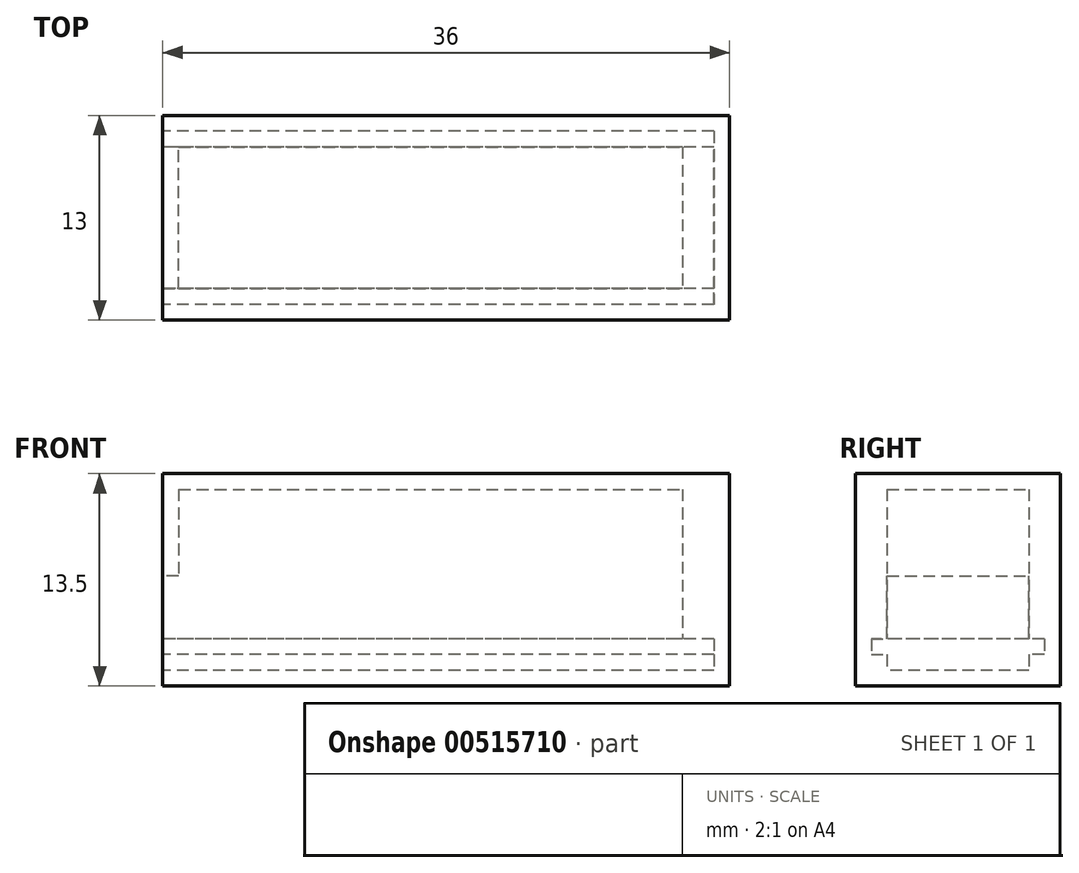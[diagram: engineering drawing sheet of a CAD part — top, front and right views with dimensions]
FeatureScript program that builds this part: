
annotation { "Feature Type Name" : "Feature", "Feature Type Description" : "" }
export const myFeature = defineFeature(function(context is Context, id is Id, definition is map)
    precondition{}
    {
        {
            var Q0;
            Q0=qCreatedBy(makeId("Top.planeOp"),FACE);
            var sketch = newSketch(context, id + "F0", { "sketchPlane" : qUnion([Q0])});
            skLineSegment(sketch, "E0.bottom", {"start": v(-27.77, -4.5) * mm, "end": v(4.23, -4.5) * mm});
            skLineSegment(sketch, "E0.top", {"start": v(-27.77, 4.5) * mm, "end": v(4.23, 4.5) * mm});
            skLineSegment(sketch, "E0.left", {"start": v(-27.77, -4.5) * mm, "end": v(-27.77, 4.5) * mm});
            skLineSegment(sketch, "E0.right", {"start": v(4.23, -4.5) * mm, "end": v(4.23, 4.5) * mm});
            skLineSegment(sketch, "E1.bottom", {"start": v(-28.77, -6.5) * mm, "end": v(7.23, -6.5) * mm});
            skLineSegment(sketch, "E1.top", {"start": v(-28.77, 6.5) * mm, "end": v(7.23, 6.5) * mm});
            skLineSegment(sketch, "E1.left", {"start": v(-28.77, -6.5) * mm, "end": v(-28.77, 6.5) * mm});
            skLineSegment(sketch, "E1.right", {"start": v(7.23, -6.5) * mm, "end": v(7.23, 6.5) * mm});
            skLineSegment(sketch, "E2", {"start": v(-28.77, 0) * mm, "end": v(7.23, 0) * mm, "construction": true});
            skLineSegment(sketch, "E3", {"start": v(-27.77, -4.5) * mm, "end": v(-28.77, -4.5) * mm});
            skLineSegment(sketch, "E4", {"start": v(-27.77, 4.5) * mm, "end": v(-28.77, 4.5) * mm});
            skSolve(sketch);
        }
        {
            var Q0;
            Q0=makeQuery(id+"F0.imprint","IMPRINT",FACE,{"disambiguationData":[TD([[makeQuery(id+"F0.imprint","IMPRINT",EDGE,{"derivedFrom":sQuery(id+"F0.wireOp",EDGE,"E0.bottom")}),-1.0]])]});
            var Q1;
            Q1=makeQuery(id+"F0.imprint","IMPRINT",FACE,{"disambiguationData":[TD([[makeQuery(id+"F0.imprint","IMPRINT",EDGE,{"derivedFrom":sQuery(id+"F0.wireOp",EDGE,"E0.bottom")}),1.0]])]});
            var Q2;
            Q2=makeQuery(id+"F0.imprint","IMPRINT",FACE,{"disambiguationData":[TD([[makeQuery(id+"F0.imprint","IMPRINT",EDGE,{"derivedFrom":sQuery(id+"F0.wireOp",EDGE,"E0.left")}),1.0]])]});
            extrude(context, id + "F1", {"entities" : qUnion([Q0, Q1, Q2]), "depth" : 6.5 * mm, "offsetDistance" : 25 * mm});
        }
        {
            var Q0;
            Q0=makeQuery(id+"F0.imprint","IMPRINT",FACE,{"disambiguationData":[TD([[makeQuery(id+"F0.imprint","IMPRINT",EDGE,{"derivedFrom":sQuery(id+"F0.wireOp",EDGE,"E0.bottom")}),1.0]])]});
            extrude(context, id + "F2", {"entities" : qUnion([Q0]), "operationType" : NewBodyOperationType.REMOVE, "depth" : 5.5 * mm, "offsetDistance" : 25 * mm});
        }
        {
            var Q0;
            Q0=makeQuery(id+"F0.imprint","IMPRINT",FACE,{"disambiguationData":[TD([[makeQuery(id+"F0.imprint","IMPRINT",EDGE,{"derivedFrom":sQuery(id+"F0.wireOp",EDGE,"E0.bottom")}),-1.0]])]});
            extrude(context, id + "F3", {"entities" : qUnion([Q0]), "operationType" : NewBodyOperationType.ADD, "oppositeDirection" : true, "depth" : 7 * mm, "offsetDistance" : 25 * mm});
        }
        {
            var Q0;
            {var subQ0=sQuery(id+"F0.wireOp",EDGE,"E1.left");Q0=makeQuery(id+"F3.boolean.opBoolean","MERGE",FACE,{"derivedFrom":[makeQuery(id+"F1.opExtrude","SWEPT_FACE",FACE,{"disambiguationData":[OSD([subQ0])]}),makeQuery(id+"F3.opExtrude","SWEPT_FACE",FACE,{"disambiguationData":[OSD([subQ0]),TDD([makeQuery(id+"F0.imprint","IMPRINT",EDGE,{"disambiguationData":[TD([[makeQuery(id+"F0.imprint","INTERSECT",VERTEX,{"derivedFrom":[sQuery(id+"F0.wireOp",EDGE,"E1.bottom"),subQ0]}),-1.0]])],"derivedFrom":subQ0})])]}),makeQuery(id+"F3.opExtrude","SWEPT_FACE",FACE,{"disambiguationData":[OSD([subQ0]),TDD([makeQuery(id+"F0.imprint","IMPRINT",EDGE,{"disambiguationData":[TD([[makeQuery(id+"F0.imprint","INTERSECT",VERTEX,{"derivedFrom":[sQuery(id+"F0.wireOp",EDGE,"E1.top"),subQ0]}),1.0]])],"derivedFrom":subQ0})])]})]});}
            var sketch = newSketch(context, id + "F4", { "sketchPlane" : qUnion([Q0])});
            skLineSegment(sketch, "E5.bottom", {"start": v(-5.5, -4) * mm, "end": v(-4.5, -4) * mm});
            skLineSegment(sketch, "E5.top", {"start": v(-5.5, -5) * mm, "end": v(-4.5, -5) * mm});
            skLineSegment(sketch, "E5.left", {"start": v(-5.5, -4) * mm, "end": v(-5.5, -5) * mm});
            skLineSegment(sketch, "E5.right", {"start": v(-4.5, -4) * mm, "end": v(-4.5, -5) * mm});
            skLineSegment(sketch, "E6", {"start": v(0, 0) * mm, "end": v(0, -9.1) * mm, "construction": true});
            skPoint(sketch, "E6.endSnap0", {"position": v(0, 0) * mm});
            skLineSegment(sketch, "E7.bottom", {"start": v(-4.5, -6) * mm, "end": v(4.5, -6) * mm});
            skLineSegment(sketch, "E7.top", {"start": v(-4.5, -7) * mm, "end": v(4.5, -7) * mm});
            skLineSegment(sketch, "E7.left", {"start": v(-4.5, -6) * mm, "end": v(-4.5, -7) * mm});
            skLineSegment(sketch, "E7.right", {"start": v(4.5, -6) * mm, "end": v(4.5, -7) * mm});
            skSolve(sketch);
        }
        {
            var Q0;
            Q0=makeQuery(id+"F4.imprint","IMPRINT",FACE,{"disambiguationData":[TD([[makeQuery(id+"F4.imprint","IMPRINT",EDGE,{"derivedFrom":sQuery(id+"F4.wireOp",EDGE,"E5.bottom")}),-1.0]])]});
            extrude(context, id + "F5", {"entities" : qUnion([Q0]), "operationType" : NewBodyOperationType.REMOVE, "oppositeDirection" : true, "depth" : 35 * mm, "offsetDistance" : 25 * mm});
        }
        {
            var Q0;
            Q0=makeQuery(id+"F1.opExtrude","SWEPT_BODY",BODY,{"disambiguationData":[OSD([sQuery(id+"F0.wireOp",EDGE,"E1.bottom"),sQuery(id+"F0.wireOp",EDGE,"E1.top"),sQuery(id+"F0.wireOp",EDGE,"E1.left"),sQuery(id+"F0.wireOp",EDGE,"E1.right")])]});
            var Q1;
            Q1=qCreatedBy(makeId("Front.planeOp"),FACE);
            mirror(context, id + "F6", {"operationType" : NewBodyOperationType.INTERSECT, "entities" : qUnion([Q0]), "mirrorPlane" : qUnion([Q1])});
        }
        {
            var Q0;
            {var subQ0=sQuery(id+"F0.wireOp",EDGE,"E0.right");Q0=makeQuery(id+"F3.boolean.opBoolean","MERGE",FACE,{"derivedFrom":[makeQuery(id+"F2.boolean.opBoolean","COPY",FACE,{"derivedFrom":makeQuery(id+"F2.opExtrude","SWEPT_FACE",FACE,{"disambiguationData":[OSD([subQ0])]})}),makeQuery(id+"F3.opExtrude","SWEPT_FACE",FACE,{"disambiguationData":[OSD([subQ0])]})]});}
            var sketch = newSketch(context, id + "F7", { "sketchPlane" : qUnion([Q0])});
            skLineSegment(sketch, "E8.bottom", {"start": v(-4.5, -4) * mm, "end": v(4.5, -4) * mm});
            skLineSegment(sketch, "E8.top", {"start": v(-4.5, -7) * mm, "end": v(4.5, -7) * mm});
            skLineSegment(sketch, "E8.left", {"start": v(-4.5, -4) * mm, "end": v(-4.5, -7) * mm});
            skLineSegment(sketch, "E8.right", {"start": v(4.5, -4) * mm, "end": v(4.5, -7) * mm});
            skSolve(sketch);
        }
        {
            var Q0;
            {var subQ3=sQuery(id+"F7.wireOp",EDGE,"E8.bottom");Q0=makeQuery(id+"F7.imprint","IMPRINT",FACE,{"disambiguationData":[TD([[makeQuery(id+"F7.imprint","IMPRINT",EDGE,{"derivedFrom":subQ3}),-1.0]])]});}
            extrude(context, id + "F8", {"entities" : qUnion([Q0]), "operationType" : NewBodyOperationType.REMOVE, "oppositeDirection" : true, "depth" : 2 * mm, "offsetDistance" : 25 * mm});
        }
        {
            var Q0;
            Q0=makeQuery(id+"F4.imprint","IMPRINT",FACE,{"disambiguationData":[TD([[makeQuery(id+"F4.imprint","IMPRINT",EDGE,{"derivedFrom":sQuery(id+"F4.wireOp",EDGE,"E7.bottom")}),-1.0]])]});
            var Q1;
            Q1=makeQuery(id+"F1.opExtrude","SWEPT_BODY",BODY,{"disambiguationData":[OSD([sQuery(id+"F0.wireOp",EDGE,"E1.bottom"),sQuery(id+"F0.wireOp",EDGE,"E1.top"),sQuery(id+"F0.wireOp",EDGE,"E1.left"),sQuery(id+"F0.wireOp",EDGE,"E1.right")])]});
            extrude(context, id + "F9", {"entities" : qUnion([Q0]), "operationType" : NewBodyOperationType.ADD, "endBound" : BoundingType.UP_TO_BODY, "oppositeDirection" : true, "depth" : 25 * mm, "endBoundEntityBody" : qUnion([Q1]), "offsetDistance" : 25 * mm});
        }
    });
